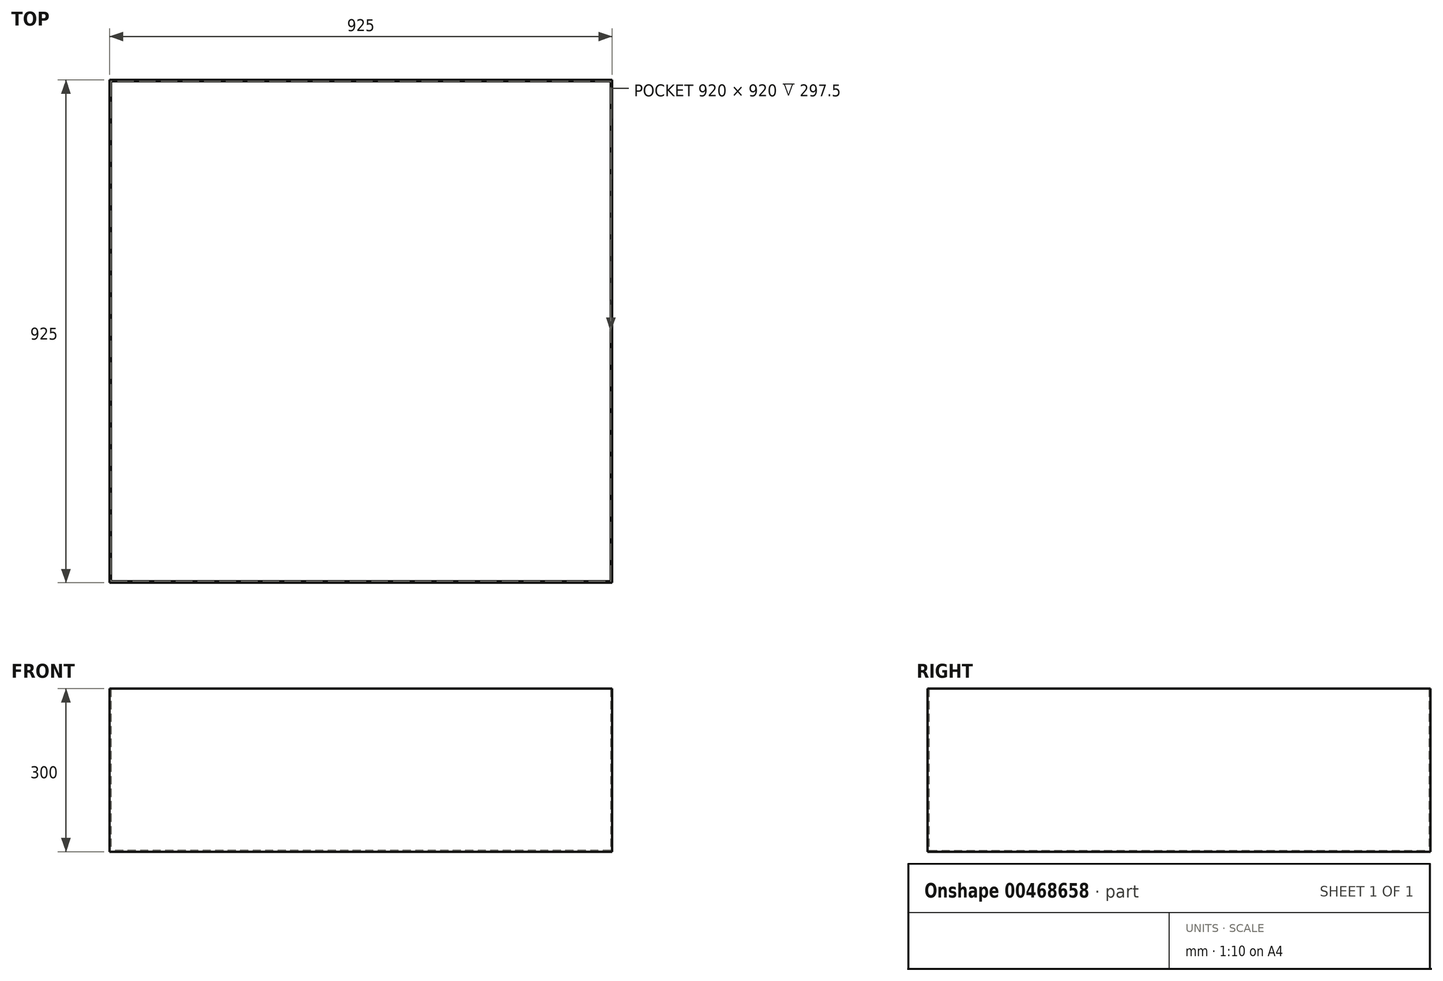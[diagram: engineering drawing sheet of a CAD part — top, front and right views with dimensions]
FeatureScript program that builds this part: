
annotation { "Feature Type Name" : "Feature", "Feature Type Description" : "" }
export const myFeature = defineFeature(function(context is Context, id is Id, definition is map)
    precondition{}
    {
        {
            var Q0;
            Q0=qCreatedBy(makeId("Top.planeOp"),FACE);
            var sketch = newSketch(context, id + "F0", { "sketchPlane" : qUnion([Q0]) });
            skLineSegment(sketch, "E0.bottom", {"start": v(462.5, -462.5) * mm, "end": v(-462.5, -462.5) * mm});
            skLineSegment(sketch, "E0.top", {"start": v(462.5, 462.5) * mm, "end": v(-462.5, 462.5) * mm});
            skLineSegment(sketch, "E0.left", {"start": v(462.5, -462.5) * mm, "end": v(462.5, 462.5) * mm});
            skLineSegment(sketch, "E0.right", {"start": v(-462.5, -462.5) * mm, "end": v(-462.5, 462.5) * mm});
            skPoint(sketch, "E0.middle", {"position": v(0, 0) * mm});
            skSolve(sketch);
        }
        {
            var Q0;
            Q0=qSketchRegion(id+"F0",true);
            extrude(context, id + "F1", {"entities" : qUnion([Q0]), "depth" : 300 * mm, "offsetDistance" : 25 * mm});
        }
        {
            var Q0;
            Q0=makeQuery(id+"F1.opExtrude","CAP_FACE",FACE,{"disambiguationData":[OSD([sQuery(id+"F0.wireOp",EDGE,"E0.bottom"),sQuery(id+"F0.wireOp",EDGE,"E0.top"),sQuery(id+"F0.wireOp",EDGE,"E0.left"),sQuery(id+"F0.wireOp",EDGE,"E0.right")])],"isStart":false});
            shell(context, id + "F2", {"entities" : qUnion([Q0]), "thickness" : 2.5 * mm});
        }
    });
